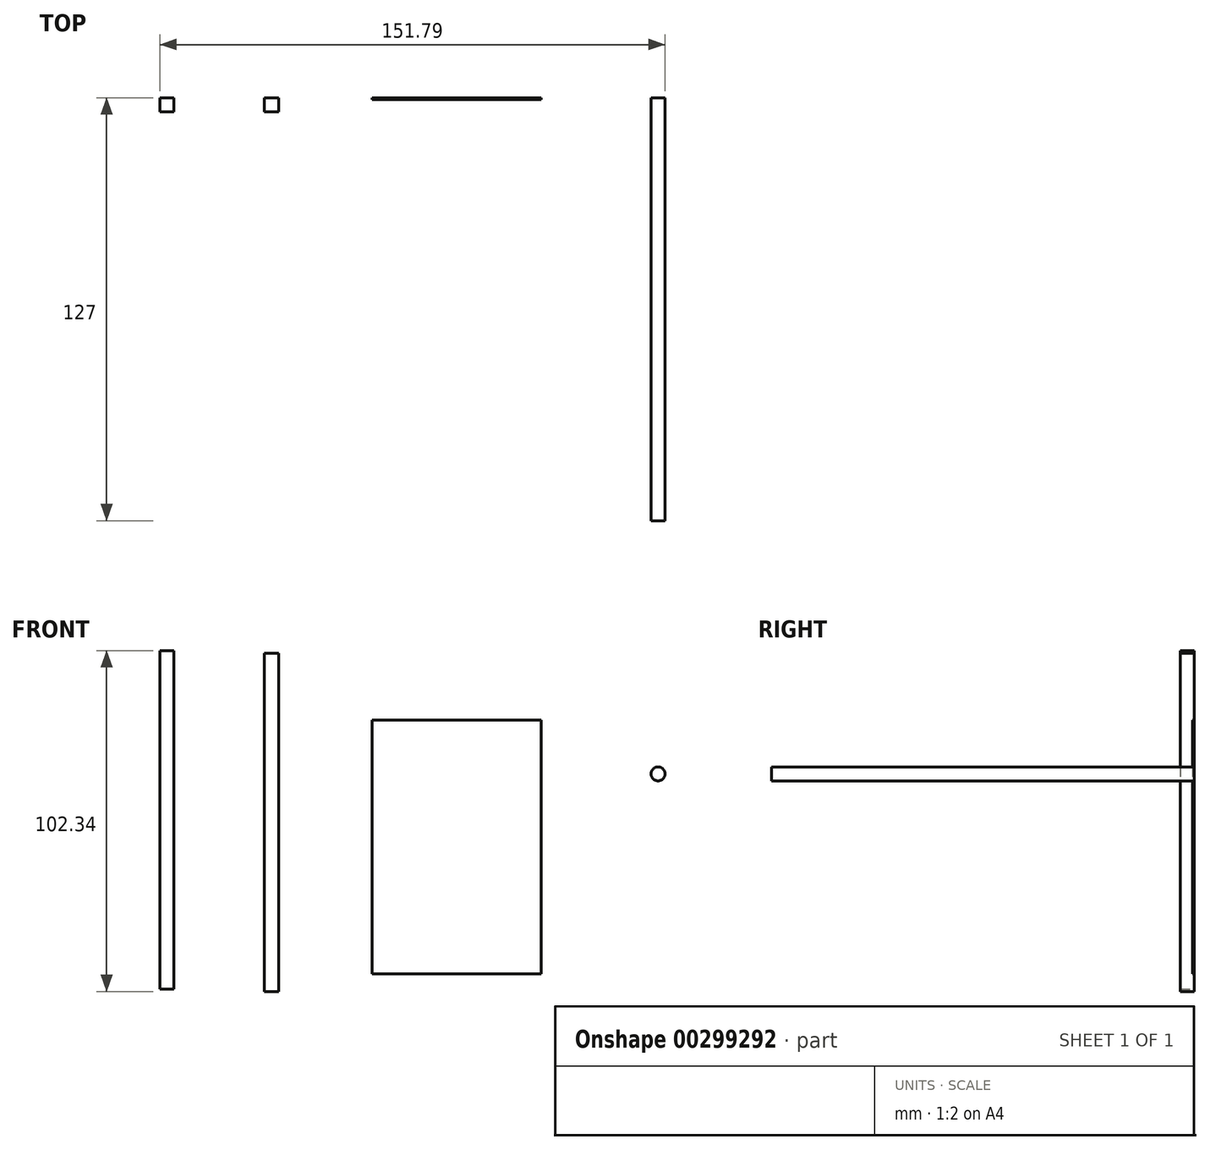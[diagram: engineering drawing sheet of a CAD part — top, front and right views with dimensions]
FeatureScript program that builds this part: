
annotation { "Feature Type Name" : "Feature", "Feature Type Description" : "" }
export const myFeature = defineFeature(function(context is Context, id is Id, definition is map)
    precondition{}
    {
        {
            var Q0;
            Q0=qCreatedBy(makeId("Front.planeOp"),FACE);
            var sketch = newSketch(context, id + "F0", { "sketchPlane" : qUnion([Q0])});
            skLineSegment(sketch, "E0", {"start": v(-25.4, 56.06) * mm, "end": v(-25.4, -20.14) * mm});
            skLineSegment(sketch, "E1", {"start": v(25.4, 56.06) * mm, "end": v(25.4, -20.14) * mm});
            skLineSegment(sketch, "E2", {"start": v(-25.4, -20.14) * mm, "end": v(25.4, -20.14) * mm});
            skLineSegment(sketch, "E3", {"start": v(-25.4, 56.06) * mm, "end": v(25.4, 56.06) * mm});
            skLineSegment(sketch, "E4", {"start": v(-89.12, 76.9) * mm, "end": v(-89.12, -24.7) * mm});
            skLineSegment(sketch, "E5", {"start": v(-89.12, -24.7) * mm, "end": v(-84.89, -24.7) * mm});
            skLineSegment(sketch, "E6", {"start": v(-84.89, -24.7) * mm, "end": v(-84.89, 76.9) * mm});
            skLineSegment(sketch, "E7", {"start": v(-84.89, 76.9) * mm, "end": v(-89.12, 76.9) * mm});
            skLineSegment(sketch, "E8.bottom", {"start": v(-57.68, 76.16) * mm, "end": v(-53.44, 76.16) * mm});
            skLineSegment(sketch, "E8.top", {"start": v(-57.68, -25.44) * mm, "end": v(-53.44, -25.44) * mm});
            skLineSegment(sketch, "E8.left", {"start": v(-57.68, 76.16) * mm, "end": v(-57.68, -25.44) * mm});
            skLineSegment(sketch, "E8.right", {"start": v(-53.44, 76.16) * mm, "end": v(-53.44, -25.44) * mm});
            skSolve(sketch);
        }
        {
            var Q0;
            Q0=makeQuery(id+"F0.imprint","IMPRINT",FACE,{"disambiguationData":[TD([[makeQuery(id+"F0.imprint","IMPRINT",EDGE,{"derivedFrom":sQuery(id+"F0.wireOp",EDGE,"E4")}),1.0]])]});
            extrude(context, id + "F1", {"entities" : qUnion([Q0]), "depth" : 4.24 * mm});
        }
        {
            var Q0;
            Q0=makeQuery(id+"F0.imprint","IMPRINT",FACE,{"disambiguationData":[TD([[makeQuery(id+"F0.imprint","IMPRINT",EDGE,{"derivedFrom":sQuery(id+"F0.wireOp",EDGE,"E0")}),1.0]])]});
            extrude(context, id + "F2", {"entities" : qUnion([Q0]), "depth" : 0.53 * mm});
        }
        {
            var Q0;
            Q0=qCreatedBy(makeId("Front.planeOp"),FACE);
            var sketch = newSketch(context, id + "F3", { "sketchPlane" : qUnion([Q0])});
            skCircle(sketch, "E9", {"center": v(60.57, 39.89) * mm, "radius": 2.1 * mm});
            skSolve(sketch);
        }
        {
            var Q0;
            Q0=makeQuery(id+"F3.imprint","IMPRINT",FACE,{"disambiguationData":[TD([[makeQuery(id+"F3.imprint","IMPRINT",EDGE,{"derivedFrom":sQuery(id+"F3.wireOp",EDGE,"E9")}),1.0]])]});
            extrude(context, id + "F4", {"entities" : qUnion([Q0]), "depth" : 127 * mm});
        }
        {
            var Q0;
            Q0=makeQuery(id+"F0.imprint","IMPRINT",FACE,{"disambiguationData":[TD([[makeQuery(id+"F0.imprint","IMPRINT",EDGE,{"derivedFrom":sQuery(id+"F0.wireOp",EDGE,"E8.bottom")}),-1.0]])]});
            extrude(context, id + "F5", {"entities" : qUnion([Q0]), "depth" : 4.24 * mm});
        }
    });
